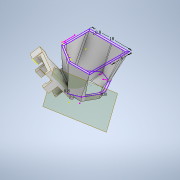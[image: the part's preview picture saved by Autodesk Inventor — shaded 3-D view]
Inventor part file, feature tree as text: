
AUTODESK INVENTOR PART (.ipt)
format: ipt  version: 2022 (Build 260153000, 153)  size: 538,112 bytes
history: native  units: in
note: dims shown in document units (in); Inventor stores cm internally (conversion verified against a paired STEP export)
features: sketch x10, plane x5, other x4, loft x4, extrude x1, split x1, move_body x1, revolve x1
ambient origin geometry x8: Origin, YZ Plane, XZ Plane, XY Plane, X Axis, Y Axis, Z Axis, Center Point
bodies: Solid1 (feature_tree)
feature tree (27):
  sketch  "Sketch1"  dims[d0=0.2441in d1=60.0deg]
  plane  "Work Plane1"
  plane  "Work Plane2"
  sketch  "Sketch2"  dims[d2=0.1063in d3=0.202in]
  other  "Repaired Geometry1"
  extrude  "Extrusion3"  TaperAngle=60.0deg  [1 undecoded]
  plane  "Work Plane5"
  sketch  "Sketch4"  dims[d8=0.0315in d11=0.1181in]
  plane  "Work Plane3"
  split  "Split3"
  sketch  "Sketch5"  dims[d14=0.0315in d15=0.0315in]
  plane  "Work Plane4"
  sketch  "Sketch6"  dims[d20=0.1181in d27=0.1181in d28=0.1181in d29=0.0in d30=0.0in]
  loft  "Loft3"
  other  "cam_holder_new_module"
  sketch  "Sketch7"  dims[d33=0.3937in]
  loft  "Loft5"
  move_body  "Move Body3"
  sketch  "Sketch9"  dims[d36=0.0315in]
  revolve  "Revolution1"  [1 undecoded]
  loft  "Loft9"
  loft  "Loft10"
  sketch  "Sketch11"  dims[d44=0.3543in d45=0.7087in d48=0.0315in d57=0.0in d58=90.0deg d59=0.0in d60=90.0deg d73=0.0933in d74=0.0315in d75=0.0984in d76=0.0591in d77=0.0591in d78=0.0in d79=90.0deg d80=0.0in d81=90.0deg d84=30.0deg d88=-0.2474in d89=-0.3125in d90=0.0394in d91=-0.1535in d100=0.3779in d105=0.0in d106=90.0deg d107=0.0in d108=90.0deg d109=0.0in d110=90.0deg d111=0.0in d112=90.0deg d101=0.0197in d102=0.0344in d103=0.0197in d104=0.0344in]
  sketch  "Sketch3"  dims[d4=0.1181in d7=0.0315in]
  sketch  "Sketch10"  dims[d40=0.6299in]
  other  "Composite1"
  other  "Srf1"
note: 2 required parameter values undecoded (feature->parameter linkage not recoverable at this tier; creation-order binding heuristic only, values carry confidence <= 0.55)